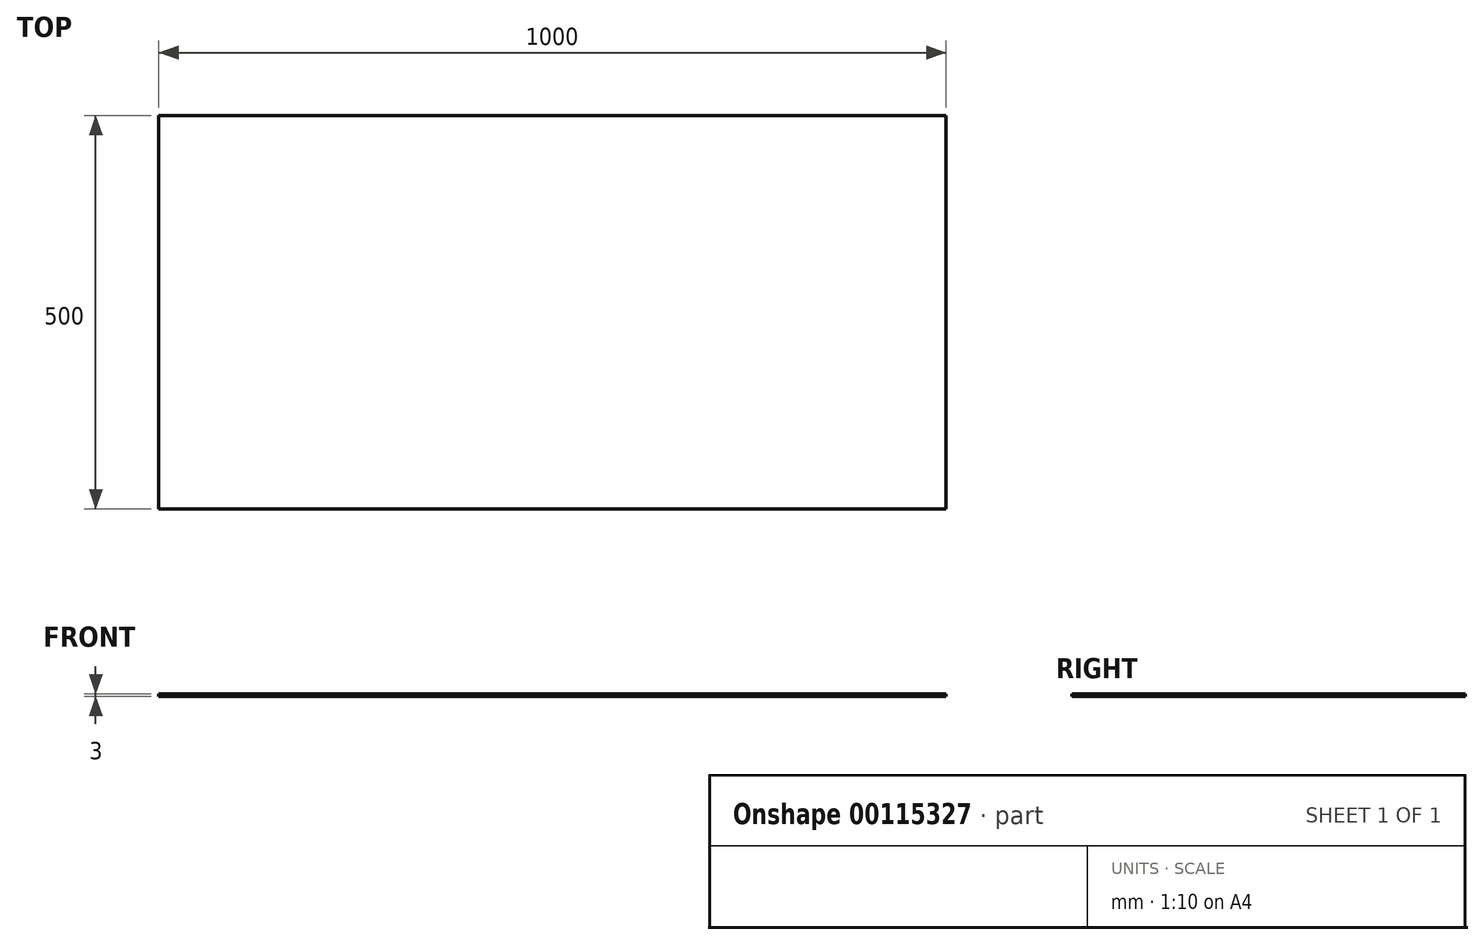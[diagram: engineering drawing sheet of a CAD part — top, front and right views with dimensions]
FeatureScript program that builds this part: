
annotation { "Feature Type Name" : "Feature", "Feature Type Description" : "" }
export const myFeature = defineFeature(function(context is Context, id is Id, definition is map)
    precondition{}
    {
        {
            var Q0;
            Q0=qCreatedBy(makeId("Top.planeOp"),FACE);
            var sketch = newSketch(context, id + "F0", { "sketchPlane" : qUnion([Q0])});
            skLineSegment(sketch, "E0.bottom", {"start": v(0, 0) * mm, "end": v(1000, 0) * mm});
            skLineSegment(sketch, "E0.top", {"start": v(0, 500) * mm, "end": v(1000, 500) * mm});
            skLineSegment(sketch, "E0.left", {"start": v(0, 0) * mm, "end": v(0, 500) * mm});
            skLineSegment(sketch, "E0.right", {"start": v(1000, 0) * mm, "end": v(1000, 500) * mm});
            skSolve(sketch);
        }
        {
            var Q0;
            Q0=qSketchRegion(id+"F0",true);
            extrude(context, id + "F1", {"entities" : qUnion([Q0]), "depth" : 3 * mm});
        }
    });
